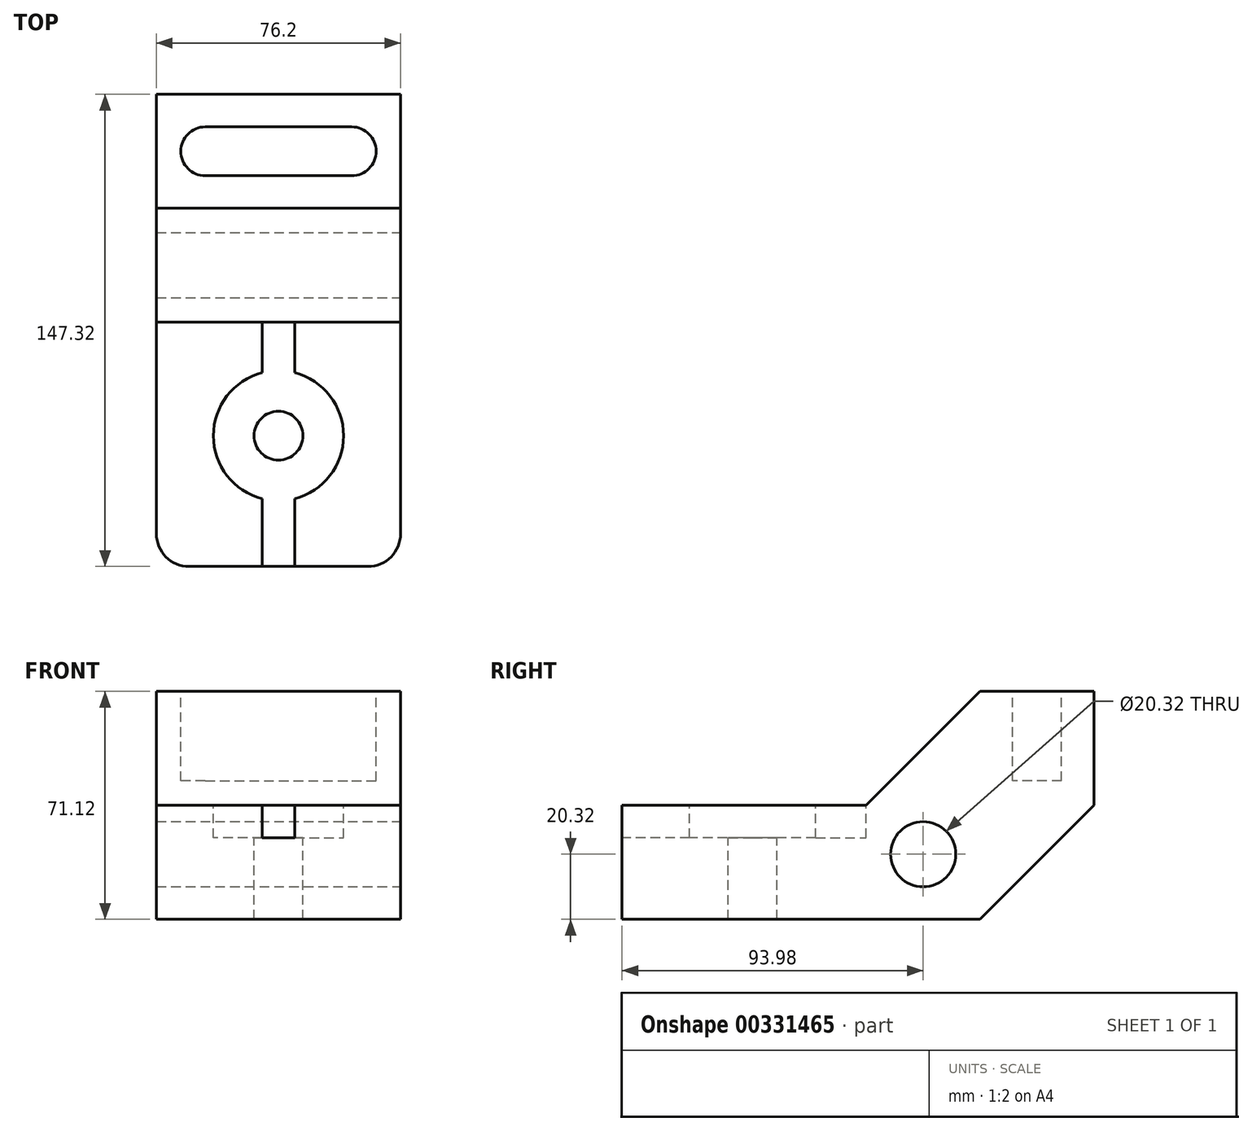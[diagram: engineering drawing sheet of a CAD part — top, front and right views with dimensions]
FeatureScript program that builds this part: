
annotation { "Feature Type Name" : "Feature", "Feature Type Description" : "" }
export const myFeature = defineFeature(function(context is Context, id is Id, definition is map)
    precondition{}
    {
        {
            var Q0;
            Q0=qCreatedBy(makeId("Right.planeOp"),FACE);
            var sketch = newSketch(context, id + "F0", { "sketchPlane" : qUnion([Q0])});
            skLineSegment(sketch, "E0", {"start": v(0, 0) * mm, "end": v(111.76, 0) * mm});
            skLineSegment(sketch, "E1", {"start": v(111.76, 0) * mm, "end": v(147.32, 35.56) * mm});
            skLineSegment(sketch, "E2", {"start": v(147.32, 35.56) * mm, "end": v(147.32, 71.12) * mm});
            skLineSegment(sketch, "E3", {"start": v(147.32, 71.12) * mm, "end": v(111.76, 71.12) * mm});
            skLineSegment(sketch, "E4", {"start": v(111.76, 71.12) * mm, "end": v(76.2, 35.56) * mm});
            skLineSegment(sketch, "E5", {"start": v(76.2, 35.56) * mm, "end": v(0, 35.56) * mm});
            skLineSegment(sketch, "E6", {"start": v(0, 35.56) * mm, "end": v(0, 0) * mm});
            skSolve(sketch);
        }
        {
            var Q0;
            Q0 = qSketchRegion(id + "F0", true);
            extrude(context, id + "F1", {"entities" : qUnion([Q0]), "depth" : 76.2 * mm});
        }
        {
            var Q0;
            Q0=makeQuery(id+"F1.opExtrude","SWEPT_FACE",FACE,{"disambiguationData":[OSD([sQuery(id+"F0.wireOp",EDGE,"E5")])]});
            var sketch = newSketch(context, id + "F2", { "sketchPlane" : qUnion([Q0])});
            skArc(sketch, "E7", {"start": v(33.02, 60.45) * mm, "mid": v(17.78, 40.78) * mm, "end": v(33.02, 21.1) * mm});
            skPoint(sketch, "E7.centerSnap0", {"position": v(38.1, 76.2) * mm});
            skLineSegment(sketch, "E8", {"start": v(33.02, 21.1) * mm, "end": v(33.02, 0) * mm});
            skLineSegment(sketch, "E9", {"start": v(33.02, 60.45) * mm, "end": v(33.02, 76.2) * mm});
            skLineSegment(sketch, "E10", {"start": v(43.18, 0) * mm, "end": v(43.18, 21.1) * mm});
            skLineSegment(sketch, "E11", {"start": v(43.18, 60.45) * mm, "end": v(43.18, 76.2) * mm});
            skArc(sketch, "E12.trimOffspring", {"start": v(43.18, 21.1) * mm, "mid": v(58.42, 40.78) * mm, "end": v(43.18, 60.45) * mm});
            skSolve(sketch);
        }
        {
            var Q0;
            Q0=sQuery(id+"F2.wireOp",VERTEX,"E7.center");
            var Q1;
            Q1=makeQuery(id+"F1.opExtrude","SWEPT_BODY",BODY,{"disambiguationData":[OSD([sQuery(id+"F0.wireOp",EDGE,"E0"),sQuery(id+"F0.wireOp",EDGE,"E1"),sQuery(id+"F0.wireOp",EDGE,"E2"),sQuery(id+"F0.wireOp",EDGE,"E3"),sQuery(id+"F0.wireOp",EDGE,"E4"),sQuery(id+"F0.wireOp",EDGE,"E5"),sQuery(id+"F0.wireOp",EDGE,"E6")])]});
            hole(context, id + "F3", {"style" : HoleStyle.C_BORE, "endStyle" : HoleEndStyle.THROUGH, "holeDiameter" : 15.24 * mm, "cBoreDiameter" : 40.64 * mm, "cBoreDepth" : 10.16 * mm, "tappedDepth" : 12.7 * mm, "tapClearance" : 3, "locations" : qUnion([Q0]), "scope" : qUnion([Q1])});
        }
        {
            var Q0;
            Q0=makeQuery(id+"F2.imprint","IMPRINT",FACE,{"disambiguationData":[TD([[makeQuery(id+"F2.imprint","IMPRINT",EDGE,{"derivedFrom":sQuery(id+"F2.wireOp",EDGE,"E7")}),1.0]])]});
            extrude(context, id + "F4", {"entities" : qUnion([Q0]), "operationType" : NewBodyOperationType.REMOVE, "oppositeDirection" : true, "depth" : 10.16 * mm});
        }
        {
            var Q0;
            Q0=makeQuery(id+"F1.opExtrude","CAP_FACE",FACE,{"disambiguationData":[OSD([sQuery(id+"F0.wireOp",EDGE,"E0"),sQuery(id+"F0.wireOp",EDGE,"E1"),sQuery(id+"F0.wireOp",EDGE,"E2"),sQuery(id+"F0.wireOp",EDGE,"E3"),sQuery(id+"F0.wireOp",EDGE,"E4"),sQuery(id+"F0.wireOp",EDGE,"E5"),sQuery(id+"F0.wireOp",EDGE,"E6")])],"isStart":false});
            var sketch = newSketch(context, id + "F5", { "sketchPlane" : qUnion([Q0])});
            skCircle(sketch, "E13", {"center": v(93.98, 20.32) * mm, "radius": 10.16 * mm});
            skSolve(sketch);
        }
        {
            var Q0;
            Q0 = qSketchRegion(id + "F5", true);
            extrude(context, id + "F6", {"entities" : qUnion([Q0]), "operationType" : NewBodyOperationType.REMOVE, "oppositeDirection" : true, "depth" : 76.2 * mm});
        }
        {
            var Q0;
            Q0=makeQuery(id+"F1.opExtrude","SWEPT_FACE",FACE,{"disambiguationData":[OSD([sQuery(id+"F0.wireOp",EDGE,"E3")])]});
            var sketch = newSketch(context, id + "F7", { "sketchPlane" : qUnion([Q0])});
            skLineSegment(sketch, "E14", {"start": v(15.24, 137.16) * mm, "end": v(60.96, 137.16) * mm});
            skLineSegment(sketch, "E15", {"start": v(60.96, 121.92) * mm, "end": v(15.24, 121.92) * mm});
            skArc(sketch, "E16", {"start": v(15.24, 137.16) * mm, "mid": v(7.62, 129.54) * mm, "end": v(15.24, 121.92) * mm});
            skArc(sketch, "E17", {"start": v(60.96, 121.92) * mm, "mid": v(68.58, 129.54) * mm, "end": v(60.96, 137.16) * mm});
            skSolve(sketch);
        }
        {
            var Q0;
            Q0 = qSketchRegion(id + "F7", true);
            extrude(context, id + "F8", {"entities" : qUnion([Q0]), "operationType" : NewBodyOperationType.REMOVE, "oppositeDirection" : true, "depth" : 27.94 * mm});
        }
        {
            var Q0;
            Q0=makeQuery(id+"F1.opExtrude","CAP_EDGE",EDGE,{"disambiguationData":[OSD([sQuery(id+"F0.wireOp",EDGE,"E6")])],"isStart":true});
            var Q1;
            Q1=makeQuery(id+"F1.opExtrude","CAP_EDGE",EDGE,{"disambiguationData":[OSD([sQuery(id+"F0.wireOp",EDGE,"E6")])],"isStart":false});
            fillet(context, id + "F9", {"entities" : qUnion([Q0, Q1]), "radius" : 10.16 * mm, "tangentPropagation" : true, "allowEdgeOverflow" : false});
        }
    });
